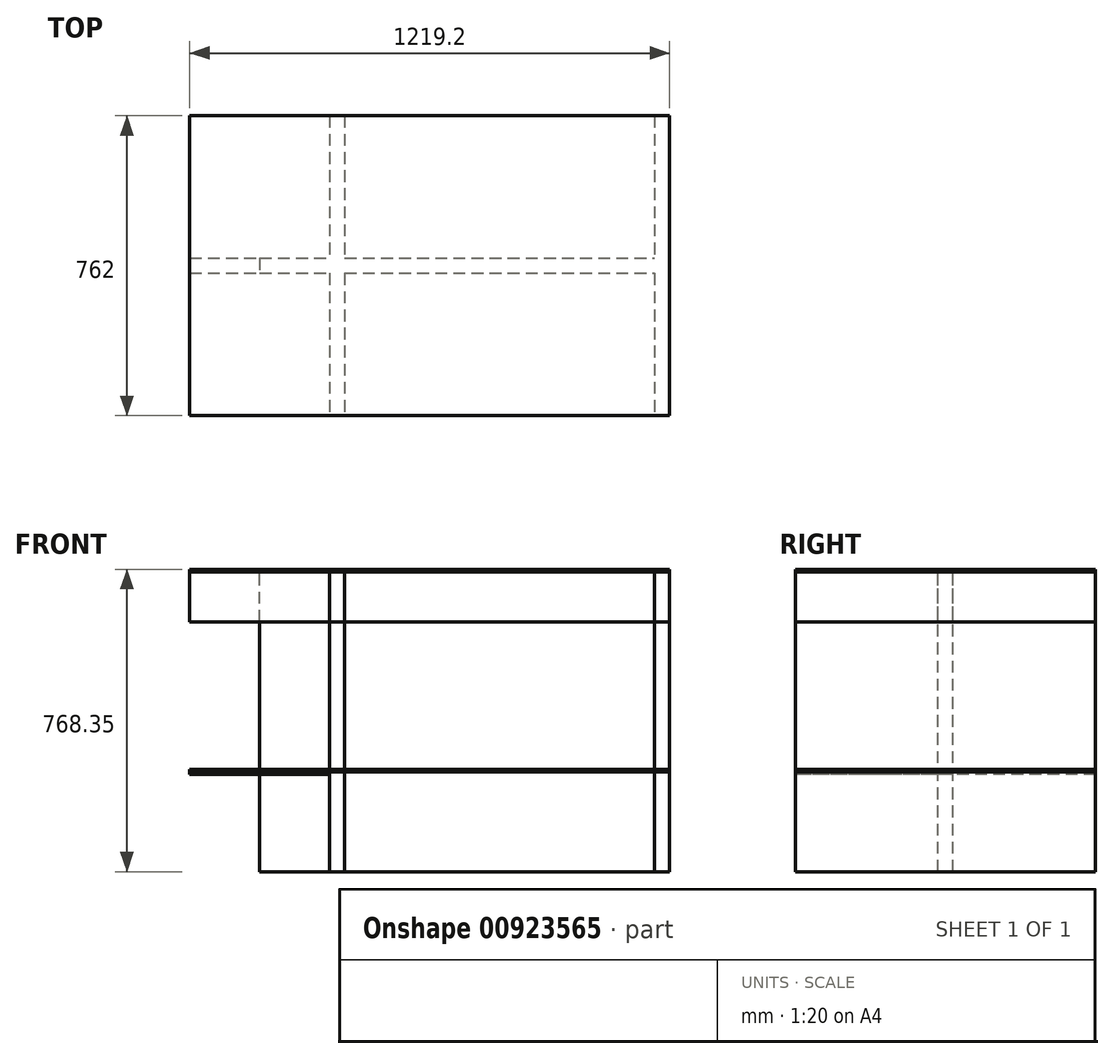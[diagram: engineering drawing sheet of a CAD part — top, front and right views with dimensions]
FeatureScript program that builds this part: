
annotation { "Feature Type Name" : "Feature", "Feature Type Description" : "" }
export const myFeature = defineFeature(function(context is Context, id is Id, definition is map)
    precondition{}
    {
        {
            var Q0;
            Q0=qCreatedBy(makeId("Top.planeOp"),FACE);
            var sketch = newSketch(context, id + "F0", { "sketchPlane" : qUnion([Q0])});
            skLineSegment(sketch, "E0.bottom", {"start": v(-1083.46, 702.01) * mm, "end": v(135.74, 702.01) * mm});
            skLineSegment(sketch, "E0.top", {"start": v(-1083.46, -59.99) * mm, "end": v(135.74, -59.99) * mm});
            skLineSegment(sketch, "E0.left", {"start": v(-1083.46, 702.01) * mm, "end": v(-1083.46, -59.99) * mm});
            skLineSegment(sketch, "E0.right", {"start": v(135.74, 702.01) * mm, "end": v(135.74, -59.99) * mm});
            skLineSegment(sketch, "E1", {"start": v(97.64, 702.01) * mm, "end": v(97.64, -59.99) * mm});
            skLineSegment(sketch, "E2.bottom", {"start": v(-727.86, 702.01) * mm, "end": v(-689.76, 702.01) * mm});
            skLineSegment(sketch, "E2.top", {"start": v(-727.86, -59.99) * mm, "end": v(-689.76, -59.99) * mm});
            skLineSegment(sketch, "E2.left", {"start": v(-727.86, 702.01) * mm, "end": v(-727.86, -59.99) * mm});
            skLineSegment(sketch, "E2.right", {"start": v(-689.76, 702.01) * mm, "end": v(-689.76, -59.99) * mm});
            skLineSegment(sketch, "E3.bottom", {"start": v(-1083.46, 340.06) * mm, "end": v(97.64, 340.06) * mm});
            skLineSegment(sketch, "E3.top", {"start": v(-1083.46, 301.96) * mm, "end": v(97.64, 301.96) * mm});
            skLineSegment(sketch, "E3.left", {"start": v(-1083.46, 340.06) * mm, "end": v(-1083.46, 301.96) * mm});
            skLineSegment(sketch, "E3.right", {"start": v(97.64, 340.06) * mm, "end": v(97.64, 301.96) * mm});
            skLineSegment(sketch, "E4", {"start": v(-905.66, 340.06) * mm, "end": v(-905.66, 301.96) * mm});
            skSolve(sketch);
        }
        {
            var Q0;
            {var subQ0=sQuery(id+"F0.wireOp",EDGE,"E2.right");var subQ1=sQuery(id+"F0.wireOp",EDGE,"E0.bottom");var subQ2=makeQuery(id+"F0.imprint","INTERSECT",VERTEX,{"derivedFrom":[subQ1,subQ0]});Q0=makeQuery(id+"F0.imprint","IMPRINT",FACE,{"disambiguationData":[TD([[makeQuery(id+"F0.imprint","IMPRINT",EDGE,{"disambiguationData":[TD([[subQ2,-1.0]])],"derivedFrom":subQ1}),-1.0]])]});}
            var Q1;
            {var subQ4=sQuery(id+"F0.wireOp",EDGE,"E0.top");var subQ6=sQuery(id+"F0.wireOp",EDGE,"E0.left");var subQ7=makeQuery(id+"F0.imprint","INTERSECT",VERTEX,{"derivedFrom":[subQ4,subQ6]});Q1=makeQuery(id+"F0.imprint","IMPRINT",FACE,{"disambiguationData":[TD([[makeQuery(id+"F0.imprint","IMPRINT",EDGE,{"disambiguationData":[TD([[subQ7,-1.0]])],"derivedFrom":subQ4}),1.0]])]});}
            var Q2;
            {var subQ0=sQuery(id+"F0.wireOp",EDGE,"E2.right");var subQ1=sQuery(id+"F0.wireOp",EDGE,"E0.top");var subQ2=makeQuery(id+"F0.imprint","INTERSECT",VERTEX,{"derivedFrom":[subQ1,subQ0]});Q2=makeQuery(id+"F0.imprint","IMPRINT",FACE,{"disambiguationData":[TD([[makeQuery(id+"F0.imprint","IMPRINT",EDGE,{"disambiguationData":[TD([[subQ2,-1.0]])],"derivedFrom":subQ1}),1.0]])]});}
            var Q3;
            {var subQ5=sQuery(id+"F0.wireOp",EDGE,"E4");Q3=makeQuery(id+"F0.imprint","IMPRINT",FACE,{"disambiguationData":[TD([[makeQuery(id+"F0.imprint","IMPRINT",EDGE,{"derivedFrom":subQ5}),-1.0]])]});}
            var Q4;
            {var subQ0=sQuery(id+"F0.wireOp",EDGE,"E3.top");var subQ1=sQuery(id+"F0.wireOp",EDGE,"E2.left");var subQ2=makeQuery(id+"F0.imprint","INTERSECT",VERTEX,{"derivedFrom":[subQ1,subQ0]});Q4=makeQuery(id+"F0.imprint","IMPRINT",FACE,{"disambiguationData":[TD([[makeQuery(id+"F0.imprint","IMPRINT",EDGE,{"disambiguationData":[TD([[subQ2,1.0]])],"derivedFrom":subQ1}),1.0]])]});}
            var Q5;
            {var subQ0=sQuery(id+"F0.wireOp",EDGE,"E2.right");var subQ1=sQuery(id+"F0.wireOp",EDGE,"E0.bottom");var subQ2=makeQuery(id+"F0.imprint","INTERSECT",VERTEX,{"derivedFrom":[subQ1,subQ0]});Q5=makeQuery(id+"F0.imprint","IMPRINT",FACE,{"disambiguationData":[TD([[makeQuery(id+"F0.imprint","IMPRINT",EDGE,{"disambiguationData":[TD([[subQ2,1.0]])],"derivedFrom":subQ1}),-1.0]])]});}
            var Q6;
            {var subQ0=sQuery(id+"F0.wireOp",EDGE,"E2.right");var subQ1=sQuery(id+"F0.wireOp",EDGE,"E0.top");var subQ2=makeQuery(id+"F0.imprint","INTERSECT",VERTEX,{"derivedFrom":[subQ1,subQ0]});Q6=makeQuery(id+"F0.imprint","IMPRINT",FACE,{"disambiguationData":[TD([[makeQuery(id+"F0.imprint","IMPRINT",EDGE,{"disambiguationData":[TD([[subQ2,1.0]])],"derivedFrom":subQ1}),1.0]])]});}
            var Q7;
            {var subQ0=sQuery(id+"F0.wireOp",EDGE,"E3.top");var subQ1=sQuery(id+"F0.wireOp",EDGE,"E1");var subQ2=makeQuery(id+"F0.imprint","INTERSECT",VERTEX,{"derivedFrom":[subQ1,subQ0]});Q7=makeQuery(id+"F0.imprint","IMPRINT",FACE,{"disambiguationData":[TD([[makeQuery(id+"F0.imprint","IMPRINT",EDGE,{"disambiguationData":[TD([[subQ2,1.0]])],"derivedFrom":subQ1}),-1.0]])]});}
            var Q8;
            {var subQ0=sQuery(id+"F0.wireOp",EDGE,"E0.right");Q8=makeQuery(id+"F0.imprint","IMPRINT",FACE,{"disambiguationData":[TD([[makeQuery(id+"F0.imprint","IMPRINT",EDGE,{"derivedFrom":subQ0}),-1.0]])]});}
            var Q9;
            {var subQ4=sQuery(id+"F0.wireOp",EDGE,"E0.bottom");var subQ6=sQuery(id+"F0.wireOp",EDGE,"E0.left");var subQ7=makeQuery(id+"F0.imprint","INTERSECT",VERTEX,{"derivedFrom":[subQ4,subQ6]});Q9=makeQuery(id+"F0.imprint","IMPRINT",FACE,{"disambiguationData":[TD([[makeQuery(id+"F0.imprint","IMPRINT",EDGE,{"disambiguationData":[TD([[subQ7,-1.0]])],"derivedFrom":subQ4}),-1.0]])]});}
            var Q10;
            {var subQ5=sQuery(id+"F0.wireOp",EDGE,"E4");Q10=makeQuery(id+"F0.imprint","IMPRINT",FACE,{"disambiguationData":[TD([[makeQuery(id+"F0.imprint","IMPRINT",EDGE,{"derivedFrom":subQ5}),1.0]])]});}
            extrude(context, id + "F1", {"entities" : qUnion([Q0, Q1, Q2, Q3, Q4, Q5, Q6, Q7, Q8, Q9, Q10]), "depth" : 6.35 * mm, "offsetDistance" : 25.4 * mm});
        }
        {
            var Q0;
            {var subQ5=sQuery(id+"F0.wireOp",EDGE,"E4");Q0=makeQuery(id+"F0.imprint","IMPRINT",FACE,{"disambiguationData":[TD([[makeQuery(id+"F0.imprint","IMPRINT",EDGE,{"derivedFrom":subQ5}),1.0]])]});}
            var Q1;
            {var subQ0=sQuery(id+"F0.wireOp",EDGE,"E2.right");var subQ1=sQuery(id+"F0.wireOp",EDGE,"E0.bottom");var subQ2=makeQuery(id+"F0.imprint","INTERSECT",VERTEX,{"derivedFrom":[subQ1,subQ0]});Q1=makeQuery(id+"F0.imprint","IMPRINT",FACE,{"disambiguationData":[TD([[makeQuery(id+"F0.imprint","IMPRINT",EDGE,{"disambiguationData":[TD([[subQ2,1.0]])],"derivedFrom":subQ1}),-1.0]])]});}
            var Q2;
            {var subQ0=sQuery(id+"F0.wireOp",EDGE,"E2.right");var subQ1=sQuery(id+"F0.wireOp",EDGE,"E0.top");var subQ2=makeQuery(id+"F0.imprint","INTERSECT",VERTEX,{"derivedFrom":[subQ1,subQ0]});Q2=makeQuery(id+"F0.imprint","IMPRINT",FACE,{"disambiguationData":[TD([[makeQuery(id+"F0.imprint","IMPRINT",EDGE,{"disambiguationData":[TD([[subQ2,1.0]])],"derivedFrom":subQ1}),1.0]])]});}
            var Q3;
            {var subQ0=sQuery(id+"F0.wireOp",EDGE,"E3.top");var subQ1=sQuery(id+"F0.wireOp",EDGE,"E2.left");var subQ2=makeQuery(id+"F0.imprint","INTERSECT",VERTEX,{"derivedFrom":[subQ1,subQ0]});Q3=makeQuery(id+"F0.imprint","IMPRINT",FACE,{"disambiguationData":[TD([[makeQuery(id+"F0.imprint","IMPRINT",EDGE,{"disambiguationData":[TD([[subQ2,1.0]])],"derivedFrom":subQ1}),1.0]])]});}
            var Q4;
            {var subQ0=sQuery(id+"F0.wireOp",EDGE,"E3.top");var subQ1=sQuery(id+"F0.wireOp",EDGE,"E1");var subQ2=makeQuery(id+"F0.imprint","INTERSECT",VERTEX,{"derivedFrom":[subQ1,subQ0]});Q4=makeQuery(id+"F0.imprint","IMPRINT",FACE,{"disambiguationData":[TD([[makeQuery(id+"F0.imprint","IMPRINT",EDGE,{"disambiguationData":[TD([[subQ2,1.0]])],"derivedFrom":subQ1}),-1.0]])]});}
            var Q5;
            {var subQ0=sQuery(id+"F0.wireOp",EDGE,"E0.right");Q5=makeQuery(id+"F0.imprint","IMPRINT",FACE,{"disambiguationData":[TD([[makeQuery(id+"F0.imprint","IMPRINT",EDGE,{"derivedFrom":subQ0}),-1.0]])]});}
            extrude(context, id + "F2", {"entities" : qUnion([Q0, Q1, Q2, Q3, Q4, Q5]), "oppositeDirection" : true, "depth" : 762 * mm, "offsetDistance" : 25.4 * mm});
        }
        {
            var Q0;
            {var subQ4=sQuery(id+"F0.wireOp",EDGE,"E0.top");var subQ6=sQuery(id+"F0.wireOp",EDGE,"E0.left");var subQ7=makeQuery(id+"F0.imprint","INTERSECT",VERTEX,{"derivedFrom":[subQ4,subQ6]});Q0=makeQuery(id+"F0.imprint","IMPRINT",FACE,{"disambiguationData":[TD([[makeQuery(id+"F0.imprint","IMPRINT",EDGE,{"disambiguationData":[TD([[subQ7,-1.0]])],"derivedFrom":subQ4}),1.0]])]});}
            var Q1;
            {var subQ5=sQuery(id+"F0.wireOp",EDGE,"E4");Q1=makeQuery(id+"F0.imprint","IMPRINT",FACE,{"disambiguationData":[TD([[makeQuery(id+"F0.imprint","IMPRINT",EDGE,{"derivedFrom":subQ5}),-1.0]])]});}
            var Q2;
            {var subQ4=sQuery(id+"F0.wireOp",EDGE,"E0.bottom");var subQ6=sQuery(id+"F0.wireOp",EDGE,"E0.left");var subQ7=makeQuery(id+"F0.imprint","INTERSECT",VERTEX,{"derivedFrom":[subQ4,subQ6]});Q2=makeQuery(id+"F0.imprint","IMPRINT",FACE,{"disambiguationData":[TD([[makeQuery(id+"F0.imprint","IMPRINT",EDGE,{"disambiguationData":[TD([[subQ7,-1.0]])],"derivedFrom":subQ4}),-1.0]])]});}
            var Q3;
            Q3=makeQuery(id+"F1.opExtrude","CAP_FACE",FACE,{"disambiguationData":[OSD([sQuery(id+"F0.wireOp",EDGE,"E0.bottom"),sQuery(id+"F0.wireOp",EDGE,"E0.top"),sQuery(id+"F0.wireOp",EDGE,"E0.left"),sQuery(id+"F0.wireOp",EDGE,"E0.right")])],"isStart":false});
            extrude(context, id + "F3", {"entities" : qUnion([Q0, Q1, Q2, Q3]), "oppositeDirection" : true, "depth" : 514.35 * mm, "offsetDistance" : 25.4 * mm, "hasSecondDirection" : true, "secondDirectionOppositeDirection" : true, "secondDirectionDepth" : 508 * mm});
        }
        {
            var Q0;
            {var subQ4=sQuery(id+"F0.wireOp",EDGE,"E0.top");var subQ6=sQuery(id+"F0.wireOp",EDGE,"E0.left");var subQ7=makeQuery(id+"F0.imprint","INTERSECT",VERTEX,{"derivedFrom":[subQ4,subQ6]});Q0=makeQuery(id+"F0.imprint","IMPRINT",FACE,{"disambiguationData":[TD([[makeQuery(id+"F0.imprint","IMPRINT",EDGE,{"disambiguationData":[TD([[subQ7,-1.0]])],"derivedFrom":subQ4}),1.0]])]});}
            var Q1;
            {var subQ4=sQuery(id+"F0.wireOp",EDGE,"E0.bottom");var subQ6=sQuery(id+"F0.wireOp",EDGE,"E0.left");var subQ7=makeQuery(id+"F0.imprint","INTERSECT",VERTEX,{"derivedFrom":[subQ4,subQ6]});Q1=makeQuery(id+"F0.imprint","IMPRINT",FACE,{"disambiguationData":[TD([[makeQuery(id+"F0.imprint","IMPRINT",EDGE,{"disambiguationData":[TD([[subQ7,-1.0]])],"derivedFrom":subQ4}),-1.0]])]});}
            var Q2;
            {var subQ0=sQuery(id+"F0.wireOp",EDGE,"E2.right");var subQ1=sQuery(id+"F0.wireOp",EDGE,"E0.bottom");var subQ2=makeQuery(id+"F0.imprint","INTERSECT",VERTEX,{"derivedFrom":[subQ1,subQ0]});Q2=makeQuery(id+"F0.imprint","IMPRINT",FACE,{"disambiguationData":[TD([[makeQuery(id+"F0.imprint","IMPRINT",EDGE,{"disambiguationData":[TD([[subQ2,-1.0]])],"derivedFrom":subQ1}),-1.0]])]});}
            var Q3;
            {var subQ0=sQuery(id+"F0.wireOp",EDGE,"E2.right");var subQ1=sQuery(id+"F0.wireOp",EDGE,"E0.top");var subQ2=makeQuery(id+"F0.imprint","INTERSECT",VERTEX,{"derivedFrom":[subQ1,subQ0]});Q3=makeQuery(id+"F0.imprint","IMPRINT",FACE,{"disambiguationData":[TD([[makeQuery(id+"F0.imprint","IMPRINT",EDGE,{"disambiguationData":[TD([[subQ2,-1.0]])],"derivedFrom":subQ1}),1.0]])]});}
            var Q4;
            {var subQ0=sQuery(id+"F0.wireOp",EDGE,"E0.right");Q4=makeQuery(id+"F0.imprint","IMPRINT",FACE,{"disambiguationData":[TD([[makeQuery(id+"F0.imprint","IMPRINT",EDGE,{"derivedFrom":subQ0}),-1.0]])]});}
            var Q5;
            {var subQ0=sQuery(id+"F0.wireOp",EDGE,"E3.top");var subQ1=sQuery(id+"F0.wireOp",EDGE,"E1");var subQ2=makeQuery(id+"F0.imprint","INTERSECT",VERTEX,{"derivedFrom":[subQ1,subQ0]});Q5=makeQuery(id+"F0.imprint","IMPRINT",FACE,{"disambiguationData":[TD([[makeQuery(id+"F0.imprint","IMPRINT",EDGE,{"disambiguationData":[TD([[subQ2,1.0]])],"derivedFrom":subQ1}),-1.0]])]});}
            var Q6;
            {var subQ0=sQuery(id+"F0.wireOp",EDGE,"E2.right");var subQ1=sQuery(id+"F0.wireOp",EDGE,"E0.top");var subQ2=makeQuery(id+"F0.imprint","INTERSECT",VERTEX,{"derivedFrom":[subQ1,subQ0]});Q6=makeQuery(id+"F0.imprint","IMPRINT",FACE,{"disambiguationData":[TD([[makeQuery(id+"F0.imprint","IMPRINT",EDGE,{"disambiguationData":[TD([[subQ2,1.0]])],"derivedFrom":subQ1}),1.0]])]});}
            var Q7;
            {var subQ0=sQuery(id+"F0.wireOp",EDGE,"E2.right");var subQ1=sQuery(id+"F0.wireOp",EDGE,"E0.bottom");var subQ2=makeQuery(id+"F0.imprint","INTERSECT",VERTEX,{"derivedFrom":[subQ1,subQ0]});Q7=makeQuery(id+"F0.imprint","IMPRINT",FACE,{"disambiguationData":[TD([[makeQuery(id+"F0.imprint","IMPRINT",EDGE,{"disambiguationData":[TD([[subQ2,1.0]])],"derivedFrom":subQ1}),-1.0]])]});}
            var Q8;
            {var subQ0=sQuery(id+"F0.wireOp",EDGE,"E3.top");var subQ1=sQuery(id+"F0.wireOp",EDGE,"E2.left");var subQ2=makeQuery(id+"F0.imprint","INTERSECT",VERTEX,{"derivedFrom":[subQ1,subQ0]});Q8=makeQuery(id+"F0.imprint","IMPRINT",FACE,{"disambiguationData":[TD([[makeQuery(id+"F0.imprint","IMPRINT",EDGE,{"disambiguationData":[TD([[subQ2,1.0]])],"derivedFrom":subQ1}),1.0]])]});}
            var Q9;
            {var subQ5=sQuery(id+"F0.wireOp",EDGE,"E4");Q9=makeQuery(id+"F0.imprint","IMPRINT",FACE,{"disambiguationData":[TD([[makeQuery(id+"F0.imprint","IMPRINT",EDGE,{"derivedFrom":subQ5}),1.0]])]});}
            var Q10;
            Q10=makeQuery(id+"F1.opExtrude","CAP_FACE",FACE,{"disambiguationData":[OSD([sQuery(id+"F0.wireOp",EDGE,"E0.bottom"),sQuery(id+"F0.wireOp",EDGE,"E0.top"),sQuery(id+"F0.wireOp",EDGE,"E0.left"),sQuery(id+"F0.wireOp",EDGE,"E0.right")])],"isStart":true});
            extrude(context, id + "F4", {"entities" : qUnion([Q0, Q1, Q2, Q3, Q4, Q5, Q6, Q7, Q8, Q9, Q10]), "oppositeDirection" : true, "depth" : 127 * mm, "offsetDistance" : 25.4 * mm});
        }
    });
